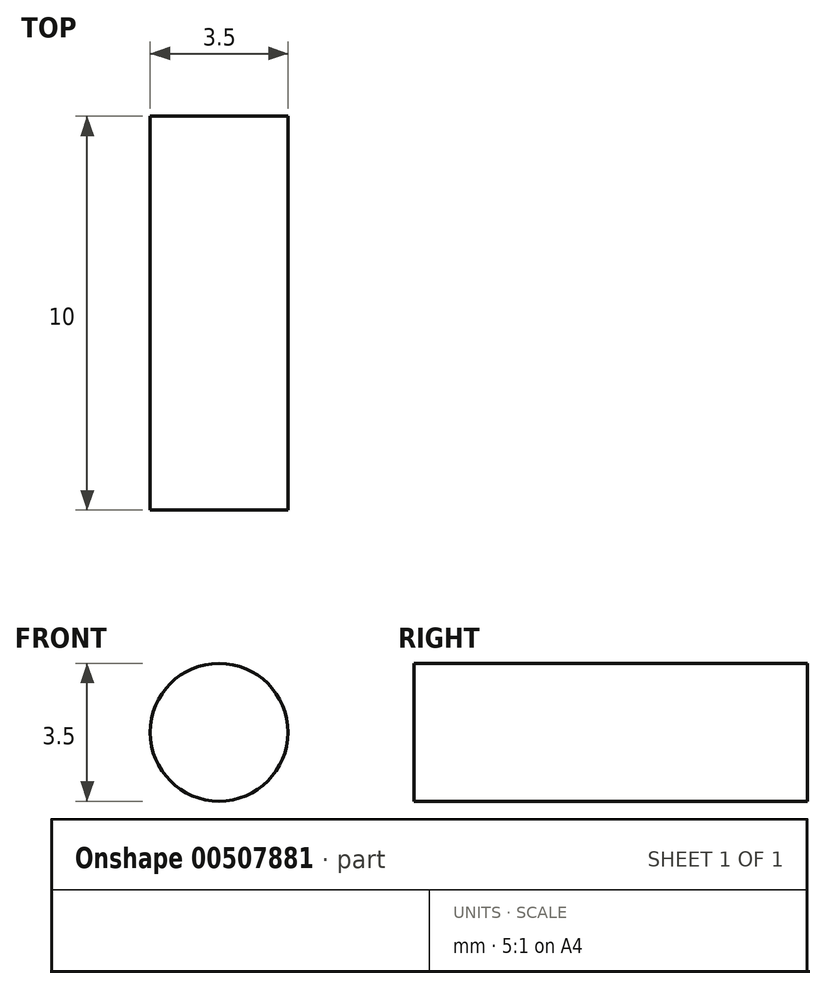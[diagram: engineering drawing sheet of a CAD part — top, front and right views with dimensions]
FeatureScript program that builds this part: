
annotation { "Feature Type Name" : "Feature", "Feature Type Description" : "" }
export const myFeature = defineFeature(function(context is Context, id is Id, definition is map)
    precondition{}
    {
        {
            var Q0;
            Q0=qCreatedBy(makeId("Front.planeOp"),FACE);
            var sketch = newSketch(context, id + "F0", { "sketchPlane" : qUnion([Q0])});
            skCircle(sketch, "E0", {"center": v(0, 0) * mm, "radius": 1.75 * mm});
            skSolve(sketch);
        }
        {
            var Q0;
            Q0=makeQuery(id+"F0.imprint","IMPRINT",FACE,{"disambiguationData":[TD([[makeQuery(id+"F0.imprint","IMPRINT",EDGE,{"derivedFrom":sQuery(id+"F0.wireOp",EDGE,"E0")}),1.0]])]});
            var Q1;
            Q1=sQuery(id+"F0.wireOp",EDGE,"E0");
            extrude(context, id + "F1", {"entities" : qUnion([Q0]), "surfaceEntities" : qUnion([Q1]), "depth" : 10 * mm, "offsetDistance" : 25 * mm, "symmetric" : true});
        }
    });
